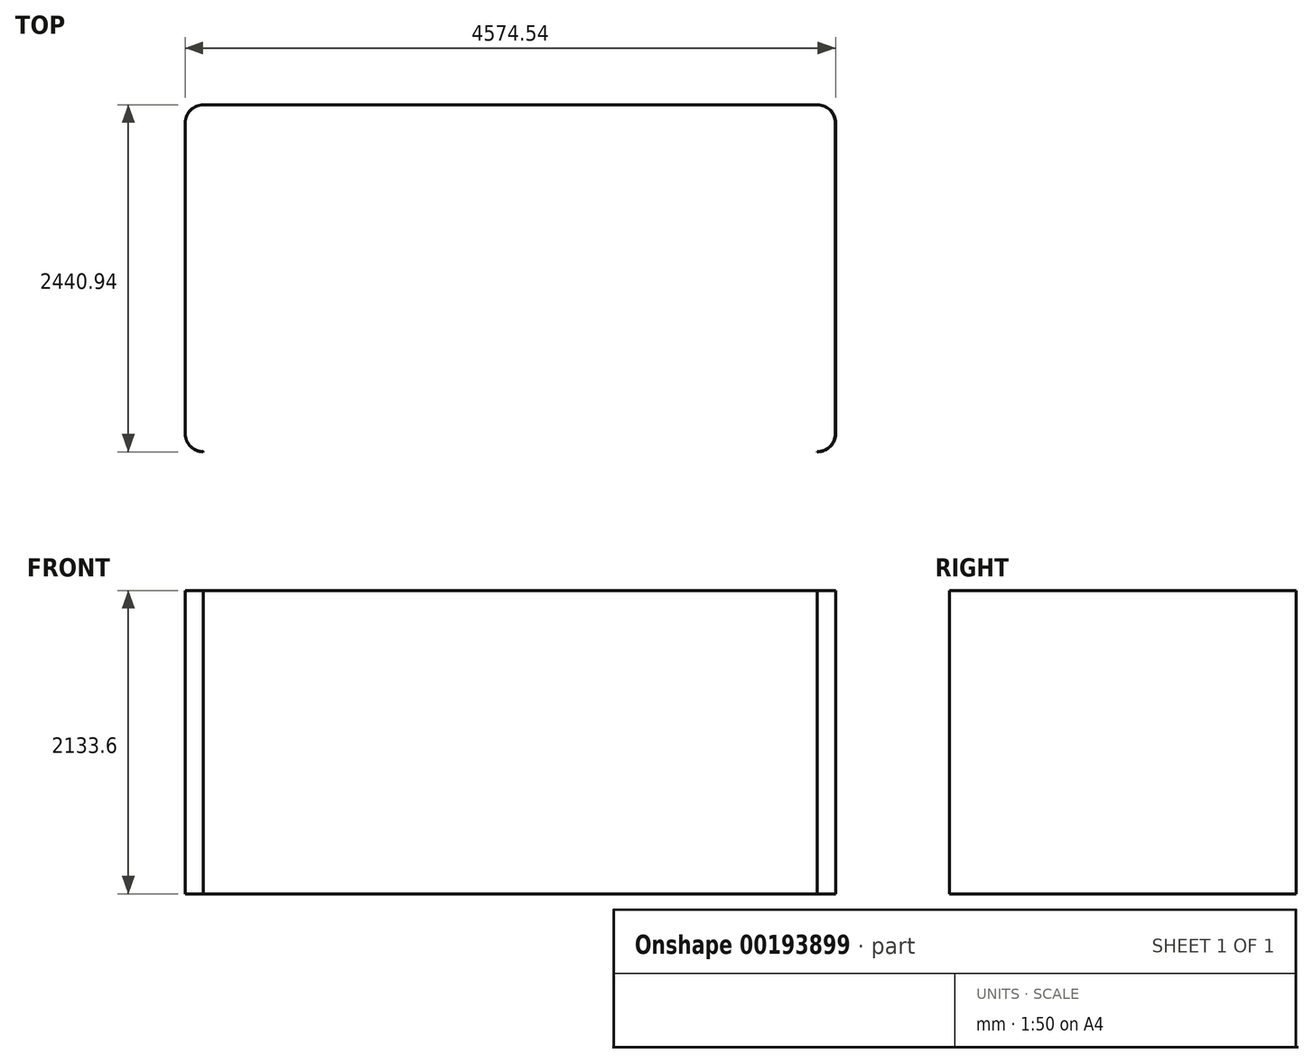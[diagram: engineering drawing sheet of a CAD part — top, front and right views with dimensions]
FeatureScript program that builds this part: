
annotation { "Feature Type Name" : "Feature", "Feature Type Description" : "" }
export const myFeature = defineFeature(function(context is Context, id is Id, definition is map)
    precondition{}
    {
        {
            var Q0;
            Q0=qCreatedBy(makeId("Top.planeOp"),FACE);
            var sketch = newSketch(context, id + "F0", { "sketchPlane" : qUnion([Q0])});
            skLineSegment(sketch, "E0.bottom", {"start": v(-2286, 1219.2) * mm, "end": v(2286, 1219.2) * mm});
            skLineSegment(sketch, "E0.top", {"start": v(-2286, -1219.2) * mm, "end": v(2286, -1219.2) * mm});
            skLineSegment(sketch, "E0.left", {"start": v(-2286, 1219.2) * mm, "end": v(-2286, -1219.2) * mm});
            skLineSegment(sketch, "E0.right", {"start": v(2286, 1219.2) * mm, "end": v(2286, -1219.2) * mm});
            skLineSegment(sketch, "E1.bottom", {"start": v(-2287.27, 1220.47) * mm, "end": v(2287.27, 1220.47) * mm});
            skLineSegment(sketch, "E1.top", {"start": v(-2287.27, -1220.47) * mm, "end": v(2287.27, -1220.47) * mm});
            skLineSegment(sketch, "E1.left", {"start": v(-2287.27, 1220.47) * mm, "end": v(-2287.27, -1220.47) * mm});
            skLineSegment(sketch, "E1.right", {"start": v(2287.27, 1220.47) * mm, "end": v(2287.27, -1220.47) * mm});
            skLineSegment(sketch, "E2", {"start": v(-2286, 1219.2) * mm, "end": v(2286, -1219.2) * mm, "construction": true});
            skLineSegment(sketch, "E3", {"start": v(-2286, -1219.2) * mm, "end": v(2286, 1219.2) * mm, "construction": true});
            skPoint(sketch, "E4", {"position": v(0, 0) * mm});
            skSolve(sketch);
        }
        {
            var Q0;
            Q0 = qSketchRegion(id + "F0", true);
            extrude(context, id + "F1", {"entities" : qUnion([Q0]), "depth" : 2438.4 * mm});
        }
        {
            var Q0;
            Q0=makeQuery(id+"F1.opExtrude","SWEPT_FACE",FACE,{"disambiguationData":[OSD([sQuery(id+"F0.wireOp",EDGE,"E1.bottom")])]});
            var sketch = newSketch(context, id + "F2", { "sketchPlane" : qUnion([Q0])});
            skLineSegment(sketch, "E5.bottom", {"start": v(2287.27, 2438.4) * mm, "end": v(-2287.27, 2438.4) * mm});
            skLineSegment(sketch, "E5.top", {"start": v(2287.27, 2133.6) * mm, "end": v(-2287.27, 2133.6) * mm});
            skLineSegment(sketch, "E5.left", {"start": v(2287.27, 2438.4) * mm, "end": v(2287.27, 2133.6) * mm});
            skLineSegment(sketch, "E5.right", {"start": v(-2287.27, 2438.4) * mm, "end": v(-2287.27, 2133.6) * mm});
            skSolve(sketch);
        }
        {
            var Q0;
            Q0=makeQuery(id+"F2.imprint","IMPRINT",FACE,{"disambiguationData":[TD([[makeQuery(id+"F2.imprint","IMPRINT",EDGE,{"derivedFrom":sQuery(id+"F2.wireOp",EDGE,"E5.bottom")}),1.0]])]});
            extrude(context, id + "F3", {"entities" : qUnion([Q0]), "operationType" : NewBodyOperationType.REMOVE, "endBound" : BoundingType.THROUGH_ALL, "oppositeDirection" : true, "depth" : 25.4 * mm});
        }
        {
            var Q0;
            Q0=makeQuery(id+"F1.opExtrude","SWEPT_EDGE",EDGE,{"disambiguationData":[OSD([sQuery(id+"F0.wireOp",EDGE,"E1.bottom"),sQuery(id+"F0.wireOp",EDGE,"E1.left")])]});
            var Q1;
            Q1=makeQuery(id+"F1.opExtrude","SWEPT_EDGE",EDGE,{"disambiguationData":[OSD([sQuery(id+"F0.wireOp",EDGE,"E0.bottom"),sQuery(id+"F0.wireOp",EDGE,"E0.left")])]});
            var Q2;
            Q2=makeQuery(id+"F1.opExtrude","SWEPT_EDGE",EDGE,{"disambiguationData":[OSD([sQuery(id+"F0.wireOp",EDGE,"E1.top"),sQuery(id+"F0.wireOp",EDGE,"E1.left")])]});
            var Q3;
            Q3=makeQuery(id+"F1.opExtrude","SWEPT_EDGE",EDGE,{"disambiguationData":[OSD([sQuery(id+"F0.wireOp",EDGE,"E0.top"),sQuery(id+"F0.wireOp",EDGE,"E0.left")])]});
            var Q4;
            Q4=makeQuery(id+"F1.opExtrude","SWEPT_EDGE",EDGE,{"disambiguationData":[OSD([sQuery(id+"F0.wireOp",EDGE,"E0.top"),sQuery(id+"F0.wireOp",EDGE,"E0.right")])]});
            var Q5;
            Q5=makeQuery(id+"F1.opExtrude","SWEPT_EDGE",EDGE,{"disambiguationData":[OSD([sQuery(id+"F0.wireOp",EDGE,"E1.top"),sQuery(id+"F0.wireOp",EDGE,"E1.right")])]});
            var Q6;
            Q6=makeQuery(id+"F1.opExtrude","SWEPT_EDGE",EDGE,{"disambiguationData":[OSD([sQuery(id+"F0.wireOp",EDGE,"E0.bottom"),sQuery(id+"F0.wireOp",EDGE,"E0.right")])]});
            var Q7;
            Q7=makeQuery(id+"F1.opExtrude","SWEPT_EDGE",EDGE,{"disambiguationData":[OSD([sQuery(id+"F0.wireOp",EDGE,"E1.bottom"),sQuery(id+"F0.wireOp",EDGE,"E1.right")])]});
            fillet(context, id + "F4", {"entities" : qUnion([Q0, Q1, Q2, Q3, Q4, Q5, Q6, Q7]), "radius" : 127 * mm, "tangentPropagation" : true, "allowEdgeOverflow" : false});
        }
        {
            var Q0;
            Q0=makeQuery(id+"F1.opExtrude","SWEPT_FACE",FACE,{"disambiguationData":[OSD([sQuery(id+"F0.wireOp",EDGE,"E0.top")])]});
            extrude(context, id + "F5", {"entities" : qUnion([Q0]), "operationType" : NewBodyOperationType.REMOVE, "oppositeDirection" : true, "depth" : 25.4 * mm});
        }
    });
